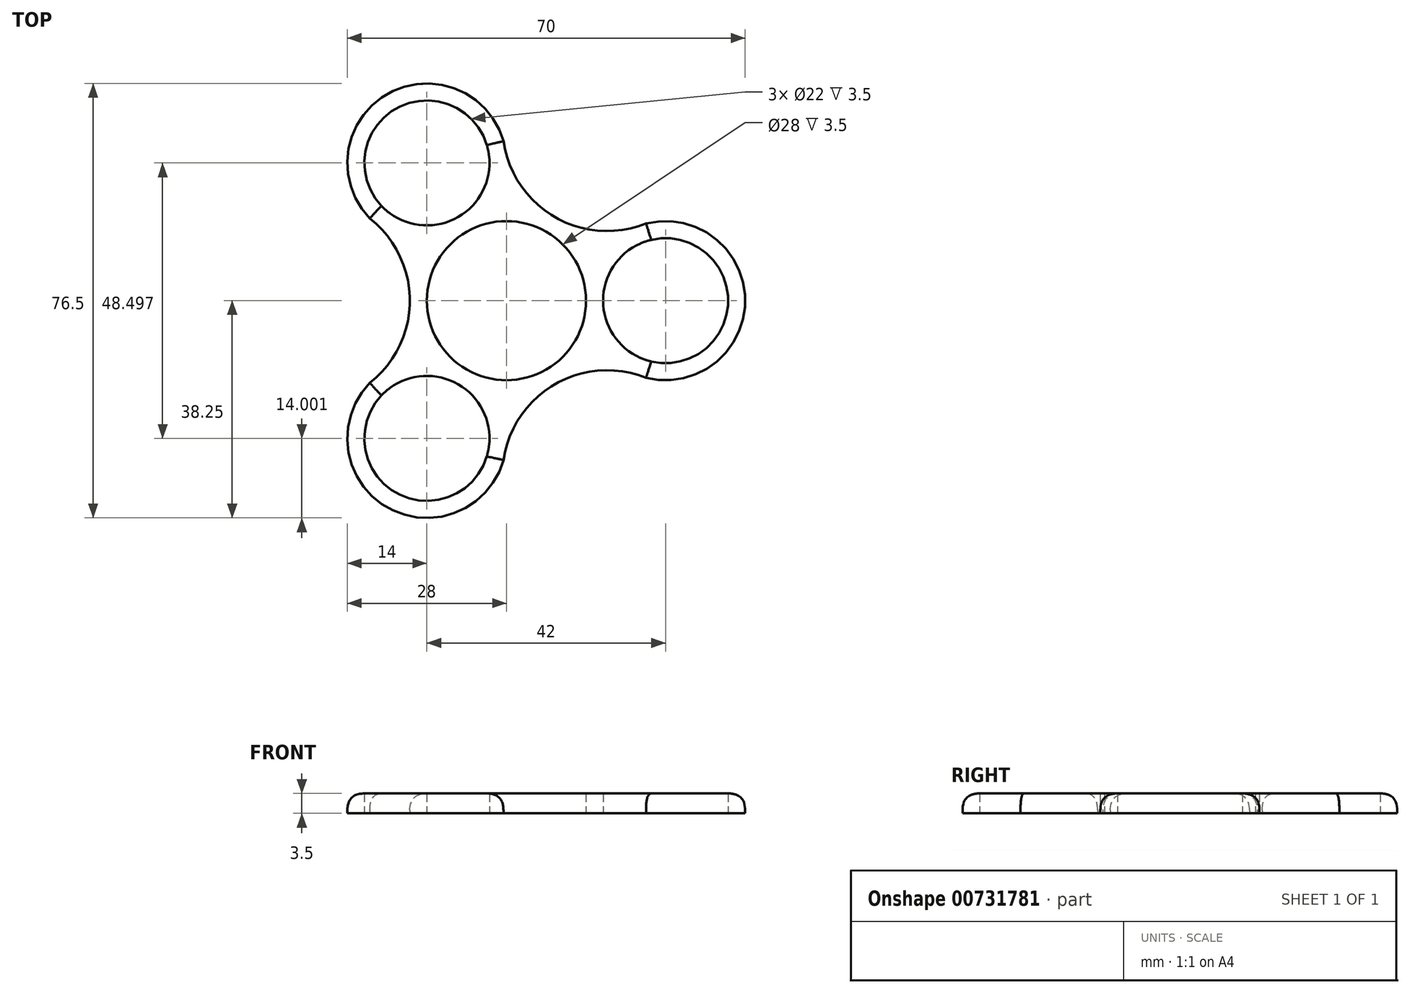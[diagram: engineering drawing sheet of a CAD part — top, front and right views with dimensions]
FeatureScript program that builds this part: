
annotation { "Feature Type Name" : "Feature", "Feature Type Description" : "" }
export const myFeature = defineFeature(function(context is Context, id is Id, definition is map)
    precondition{}
    {
        {
            var Q0;
            Q0=qCreatedBy(makeId("Top.planeOp"),FACE);
            var sketch = newSketch(context, id + "F0", { "sketchPlane" : qUnion([Q0])});
            skCircle(sketch, "E0", {"center": v(0, 0) * mm, "radius": 14 * mm});
            skLineSegment(sketch, "E1", {"start": v(14, 0) * mm, "end": v(17, 0) * mm});
            skLineSegment(sketch, "E2", {"start": v(17, 0) * mm, "end": v(28, 0) * mm});
            skCircle(sketch, "E3", {"center": v(28, 0) * mm, "radius": 11 * mm});
            skArc(sketch, "E4", {"start": v(22.57, -12.9) * mm, "mid": v(42, 0) * mm, "end": v(22.57, 12.9) * mm});
            skArc(sketch, "E5", {"start": v(-24.03, -14.48) * mm, "mid": v(-17, 0) * mm, "end": v(-24.03, 14.48) * mm});
            skArc(sketch, "E6.1.0", {"start": v(24.56, -13.57) * mm, "mid": v(8.5, -14.72) * mm, "end": v(-0.53, -28.05) * mm});
            skArc(sketch, "E6.1.1", {"start": v(-0.1, 26) * mm, "mid": v(-21, 36.37) * mm, "end": v(-22.46, 13.1) * mm});
            skCircle(sketch, "E6.1.2", {"center": v(-14, 24.25) * mm, "radius": 11 * mm});
            skArc(sketch, "E6.2.0", {"start": v(-0.53, 28.05) * mm, "mid": v(8.5, 14.72) * mm, "end": v(24.56, 13.57) * mm});
            skArc(sketch, "E6.2.1", {"start": v(-22.46, -13.1) * mm, "mid": v(-21, -36.37) * mm, "end": v(-0.1, -26) * mm});
            skCircle(sketch, "E6.2.2", {"center": v(-14, -24.25) * mm, "radius": 11 * mm});
            skSolve(sketch);
        }
        {
            var Q0;
            Q0=makeQuery(id+"F0.imprint","IMPRINT",FACE,{"disambiguationData":[TD([[makeQuery(id+"F0.imprint","IMPRINT",EDGE,{"derivedFrom":sQuery(id+"F0.wireOp",EDGE,"E0")}),-1.0]])]});
            extrude(context, id + "F1", {"entities" : qUnion([Q0]), "depth" : 3.5 * mm, "offsetDistance" : 25 * mm});
        }
        {
            var Q0;
            Q0=makeQuery(id+"F1.opExtrude","CAP_EDGE",EDGE,{"disambiguationData":[OSD([sQuery(id+"F0.wireOp",EDGE,"E6.1.0")])],"isStart":false});
            var Q1;
            Q1=makeQuery(id+"F1.opExtrude","CAP_EDGE",EDGE,{"disambiguationData":[OSD([sQuery(id+"F0.wireOp",EDGE,"E5")])],"isStart":false});
            var Q2;
            Q2=makeQuery(id+"F1.opExtrude","CAP_EDGE",EDGE,{"disambiguationData":[OSD([sQuery(id+"F0.wireOp",EDGE,"E6.2.0")])],"isStart":false});
            var Q3;
            Q3=makeQuery(id+"F1.opExtrude","CAP_EDGE",EDGE,{"disambiguationData":[OSD([sQuery(id+"F0.wireOp",EDGE,"E6.2.1")])],"isStart":false});
            var Q4;
            Q4=makeQuery(id+"F1.opExtrude","CAP_EDGE",EDGE,{"disambiguationData":[OSD([sQuery(id+"F0.wireOp",EDGE,"E4")])],"isStart":false});
            var Q5;
            Q5=makeQuery(id+"F1.opExtrude","CAP_EDGE",EDGE,{"disambiguationData":[OSD([sQuery(id+"F0.wireOp",EDGE,"E6.1.1")])],"isStart":false});
            fillet(context, id + "F2", {"entities" : qUnion([Q0, Q1, Q2, Q3, Q4, Q5]), "radius" : 3 * mm, "rho" : 0.5, "crossSection" : FilletCrossSection.CONIC, "allowEdgeOverflow" : false});
        }
    });
